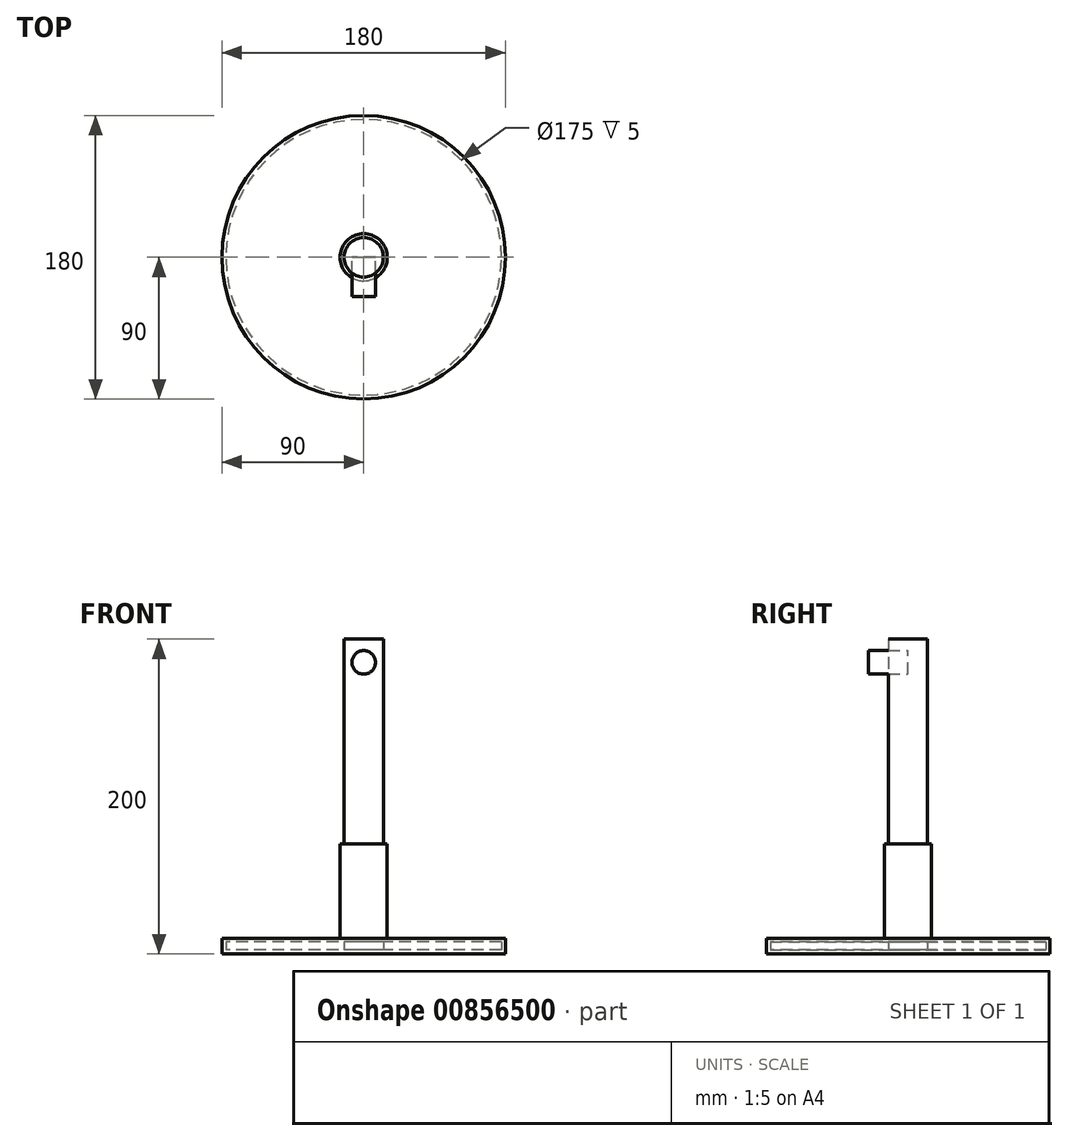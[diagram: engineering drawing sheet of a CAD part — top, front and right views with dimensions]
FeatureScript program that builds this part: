
annotation { "Feature Type Name" : "Feature", "Feature Type Description" : "" }
export const myFeature = defineFeature(function(context is Context, id is Id, definition is map)
    precondition{}
    {
        {
            var Q0;
            Q0=qCreatedBy(makeId("Top.planeOp"),FACE);
            var sketch = newSketch(context, id + "F0", { "sketchPlane" : qUnion([Q0])});
            skCircle(sketch, "E0", {"center": v(0, 0) * mm, "radius": 90 * mm});
            skSolve(sketch);
        }
        {
            var Q0;
            Q0=makeQuery(id+"F0.imprint","IMPRINT",FACE,{"disambiguationData":[TD([[makeQuery(id+"F0.imprint","IMPRINT",EDGE,{"derivedFrom":sQuery(id+"F0.wireOp",EDGE,"E0")}),1.0]])]});
            extrude(context, id + "F1", {"entities" : qUnion([Q0]), "depth" : 10 * mm, "offsetDistance" : 25 * mm});
        }
        {
            var Q0;
            Q0=qCreatedBy(makeId("Top.planeOp"),FACE);
            var sketch = newSketch(context, id + "F2", { "sketchPlane" : qUnion([Q0])});
            skCircle(sketch, "E1", {"center": v(0, 0) * mm, "radius": 15 * mm});
            skSolve(sketch);
        }
        {
            var Q0;
            Q0 = qSketchRegion(id + "F2", true);
            extrude(context, id + "F3", {"entities" : qUnion([Q0]), "operationType" : NewBodyOperationType.ADD, "depth" : 70 * mm, "offsetDistance" : 25 * mm});
        }
        {
            var Q0;
            Q0=makeQuery(id+"F3.opExtrude","CAP_FACE",FACE,{"disambiguationData":[OSD([sQuery(id+"F2.wireOp",EDGE,"E1")])],"isStart":false});
            shell(context, id + "F4", {"entities" : qUnion([Q0]), "thickness" : 2.5 * mm});
        }
        {
            var Q0;
            Q0=qCreatedBy(makeId("Top.planeOp"),FACE);
            var sketch = newSketch(context, id + "F5", { "sketchPlane" : qUnion([Q0])});
            skCircle(sketch, "E2", {"center": v(0, 0) * mm, "radius": 12.5 * mm});
            skSolve(sketch);
        }
        {
            var Q0;
            Q0 = qSketchRegion(id + "F5", true);
            extrude(context, id + "F6", {"entities" : qUnion([Q0]), "operationType" : NewBodyOperationType.ADD, "depth" : 200 * mm, "offsetDistance" : 25 * mm});
        }
        {
            var Q0;
            Q0=qCreatedBy(makeId("Front.planeOp"),FACE);
            var sketch = newSketch(context, id + "F7", { "sketchPlane" : qUnion([Q0])});
            skCircle(sketch, "E3", {"center": v(0, 185.18) * mm, "radius": 7.5 * mm});
            skSolve(sketch);
        }
        {
            var Q0;
            Q0 = qSketchRegion(id + "F7", true);
            extrude(context, id + "F8", {"entities" : qUnion([Q0]), "depth" : 25 * mm, "offsetDistance" : 25 * mm});
        }
    });
